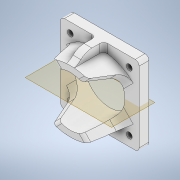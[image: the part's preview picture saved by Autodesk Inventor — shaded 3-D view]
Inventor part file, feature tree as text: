
AUTODESK INVENTOR PART (.ipt)
format: ipt  version: 2020 (Build 240168000, 168)  size: 367,104 bytes
history: native  units: mm
features: fillet x5, other x5, sketch x4, extrude x3, reference x3, projected_geometry x3, chamfer x2, hole x1, plane x1, mirror x1, thicken_offset x1
ambient origin geometry x8: Origin, YZ Plane, XZ Plane, XY Plane, X Axis, Y Axis, Z Axis, Center Point
bodies: Solid1 (feature_tree)
feature tree (29):
  extrude  "Extrusion1"  Depth=40.0mm
  hole  "Hole1"  [1 undecoded]
  extrude  "Extrusion2"  Depth=30.0mm
  chamfer  "Chamfer1"  Distance=5.0mm
  chamfer  "Chamfer2"  Distance=5.0mm
  plane  "Work Plane1"
  mirror  "Mirror1"
  fillet  "Fillet2"  Radius=25.0mm
  fillet  "Fillet3"  Radius=15.0mm
  extrude  "Extrusion3"  Depth=4.0mm
  fillet  "Fillet4"  Radius=4.0mm
  fillet  "Fillet5"  Radius=6.0mm
  fillet  "Fillet6"  Radius=2.0mm
  thicken_offset  "Thicken1"
  sketch  "Sketch1"  dims[d0=25.2mm d1=40.0mm]
  reference  "Reference1"
  reference  "Reference2"
  reference  "Reference3"
  sketch  "Sketch2"  dims[d2=40.0mm d3=5.0mm d4=0.0mm]
  projected_geometry  "Projected Loop1"
  sketch  "Sketch3"  dims[d5=30.0mm d6=30.0mm]
  projected_geometry  "Projected Loop2"
  sketch  "Sketch4"  dims[d7=3.0mm d8=6.0mm d9=4.0mm d10=2.0mm d11=90.0deg d12=8.0mm d13=20.594885mm d14=5.0mm d15=5.0mm d16=25.0mm d17=15.0mm d18=0.0mm d19=4.0mm d20=2.0mm d21=12.217305mm d22=4.0mm d23=2.0mm d24=12.217305mm d26=6.0mm d27=2.0mm d28=4.0mm d29=60.0mm d30=10.0mm d31=0.0mm d32=8.0mm d33=2.0mm d34=2.0mm d35=0.15mm d36=0.15mm]
  projected_geometry  "Projected Loop3"
  parser-record x1  (decoder bookkeeping rows leaked as tree rows — omitted from the tree; the rows remain in map.json)
  other  "sub_leg_1.iam"
  other  "carbon_fiber_25_21_300:1"
  other  "joint_connector_5:1"
  other  "joint_connector_4:1"
note: 1 required parameter value undecoded (feature->parameter linkage not recoverable at this tier; creation-order binding heuristic only, values carry confidence <= 0.55)
note: 1 file-system path scrubbed to <path> (originals preserved in map.json)
